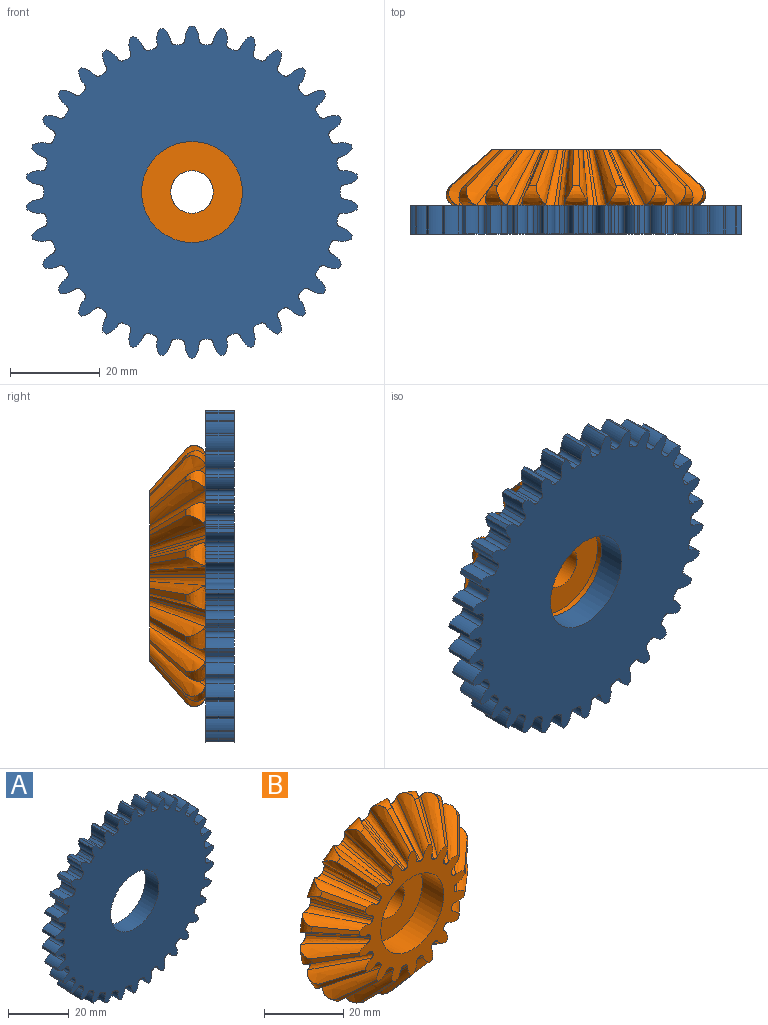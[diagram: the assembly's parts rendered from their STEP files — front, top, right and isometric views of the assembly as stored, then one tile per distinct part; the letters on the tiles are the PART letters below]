
ASSEMBLY  parts=2 mates=1
PART A: 207 faces, bbox 73.8x6.4x74 mm
  f0: cylinder r=33mm len=6.35mm, axis (0,1,0), area 7mm2, adj f34,f35,f40,f204
  f1: cylinder r=33mm len=6.35mm, axis (0,1,0), area 7mm2, adj f34,f35,f199,f205
  f2: cylinder r=33mm len=6.35mm, axis (0,1,0), area 7mm2, adj f34,f35,f194,f200
  f3: cylinder r=33mm len=6.35mm, axis (0,1,0), area 7mm2, adj f34,f35,f189,f195
  f4: cylinder r=33mm len=6.35mm, axis (0,1,0), area 7mm2, adj f34,f35,f184,f190
  f5: cylinder r=33mm len=6.35mm, axis (0,1,0), area 7mm2, adj f34,f35,f179,f185
  f6: cylinder r=33mm len=6.35mm, axis (0,1,0), area 7mm2, adj f34,f35,f174,f180
  f7: cylinder r=33mm len=6.35mm, axis (0,1,0), area 7mm2, adj f34,f35,f169,f175
  f8: cylinder r=33mm len=6.35mm, axis (0,1,0), area 7mm2, adj f34,f35,f164,f170
  f9: cylinder r=33mm len=6.35mm, axis (0,1,0), area 7mm2, adj f34,f35,f159,f165
  f10: cylinder r=33mm len=6.35mm, axis (0,1,0), area 7mm2, adj f34,f35,f154,f160
  f11: cylinder r=33mm len=6.35mm, axis (0,1,0), area 7mm2, adj f34,f35,f149,f155
  f12: cylinder r=33mm len=6.35mm, axis (0,1,0), area 7mm2, adj f34,f35,f144,f150
  f13: cylinder r=33mm len=6.35mm, axis (0,1,0), area 7mm2, adj f34,f35,f139,f145
  f14: cylinder r=33mm len=6.35mm, axis (0,1,0), area 7mm2, adj f34,f35,f134,f140
  f15: cylinder r=33mm len=6.35mm, axis (0,1,0), area 7mm2, adj f34,f35,f129,f135
  f16: cylinder r=33mm len=6.35mm, axis (0,1,0), area 7mm2, adj f34,f35,f124,f130
  f17: cylinder r=33mm len=6.35mm, axis (0,1,0), area 7mm2, adj f34,f35,f119,f125
  f18: cylinder r=33mm len=6.35mm, axis (0,1,0), area 7mm2, adj f34,f35,f114,f120
  f19: cylinder r=33mm len=6.35mm, axis (0,1,0), area 7mm2, adj f34,f35,f109,f115
  f20: cylinder r=33mm len=6.35mm, axis (0,1,0), area 7mm2, adj f34,f35,f104,f110
  f21: cylinder r=33mm len=6.35mm, axis (0,1,0), area 7mm2, adj f34,f35,f99,f105
  f22: cylinder r=33mm len=6.35mm, axis (0,1,0), area 7mm2, adj f34,f35,f94,f100
  f23: cylinder r=33mm len=6.35mm, axis (0,1,0), area 7mm2, adj f34,f35,f89,f95
  f24: cylinder r=33mm len=6.35mm, axis (0,1,0), area 7mm2, adj f34,f35,f84,f90
  f25: cylinder r=33mm len=6.35mm, axis (0,1,0), area 7mm2, adj f34,f35,f79,f85
  f26: cylinder r=33mm len=6.35mm, axis (0,1,0), area 7mm2, adj f34,f35,f74,f80
  f27: cylinder r=33mm len=6.35mm, axis (0,1,0), area 7mm2, adj f34,f35,f69,f75
  f28: cylinder r=33mm len=6.35mm, axis (0,1,0), area 7mm2, adj f34,f35,f64,f70
  f29: cylinder r=33mm len=6.35mm, axis (0,1,0), area 7mm2, adj f34,f35,f59,f65
  f30: cylinder r=33mm len=6.35mm, axis (0,1,0), area 7mm2, adj f34,f35,f54,f60
  f31: cylinder r=33mm len=6.35mm, axis (0,1,0), area 7mm2, adj f34,f35,f49,f55
  f32: cylinder r=33mm len=6.35mm, axis (0,1,0), area 7mm2, adj f34,f35,f44,f50
  f33: cylinder r=33mm len=6.35mm, axis (0,1,0), area 7mm2, adj f34,f35,f39,f45
  f34: plane 74x73.76mm, normal (0,-1,0), area 3393.5mm2, adj f0,f1,f2,f3,f4,f5,f6,f7
  f35: plane 74x73.76mm, normal (0,1,0), area 3393.5mm2, adj f0,f1,f2,f3,f4,f5,f6,f7
  f36: cylinder r=4.53mm len=6.35mm, axis (0,1,0), area 21.2mm2, adj f34,f35,f37,f40
  f37: cylinder r=37mm len=6.35mm, axis (0,1,0), area 5.8mm2, adj f34,f35,f36,f38
  f38: cylinder r=4.53mm len=6.35mm, axis (0,1,0), area 21.2mm2, adj f34,f35,f37,f39
  f39: cylinder r=1mm len=6.35mm, axis (0,1,0), area 9.6mm2, adj f33,f34,f35,f38
  f40: cylinder r=1mm len=6.35mm, axis (0,1,0), area 9.6mm2, adj f0,f34,f35,f36
  f41: cylinder r=4.53mm len=6.35mm, axis (0,1,0), area 21.2mm2, adj f34,f35,f42,f45
  f42: cylinder r=37mm len=6.35mm, axis (0,1,0), area 5.8mm2, adj f34,f35,f41,f43
  f43: cylinder r=4.53mm len=6.35mm, axis (0,1,0), area 21.2mm2, adj f34,f35,f42,f44
  f44: cylinder r=1mm len=6.35mm, axis (0,1,0), area 9.6mm2, adj f32,f34,f35,f43
  f45: cylinder r=1mm len=6.35mm, axis (0,1,0), area 9.6mm2, adj f33,f34,f35,f41
  f46: cylinder r=4.53mm len=6.35mm, axis (0,1,0), area 21.2mm2, adj f34,f35,f47,f50
  f47: cylinder r=37mm len=6.35mm, axis (0,1,0), area 5.8mm2, adj f34,f35,f46,f48
  f48: cylinder r=4.53mm len=6.35mm, axis (0,1,0), area 21.2mm2, adj f34,f35,f47,f49
  f49: cylinder r=1mm len=6.35mm, axis (0,1,0), area 9.6mm2, adj f31,f34,f35,f48
  f50: cylinder r=1mm len=6.35mm, axis (0,1,0), area 9.6mm2, adj f32,f34,f35,f46
  f51: cylinder r=4.53mm len=6.35mm, axis (0,1,0), area 21.2mm2, adj f34,f35,f52,f55
  f52: cylinder r=37mm len=6.35mm, axis (0,1,0), area 5.8mm2, adj f34,f35,f51,f53
  f53: cylinder r=4.53mm len=6.35mm, axis (0,1,0), area 21.2mm2, adj f34,f35,f52,f54
  f54: cylinder r=1mm len=6.35mm, axis (0,1,0), area 9.6mm2, adj f30,f34,f35,f53
  f55: cylinder r=1mm len=6.35mm, axis (0,1,0), area 9.6mm2, adj f31,f34,f35,f51
  f56: cylinder r=4.53mm len=6.35mm, axis (0,1,0), area 21.2mm2, adj f34,f35,f57,f60
  f57: cylinder r=37mm len=6.35mm, axis (0,1,0), area 5.8mm2, adj f34,f35,f56,f58
  f58: cylinder r=4.53mm len=6.35mm, axis (0,1,0), area 21.2mm2, adj f34,f35,f57,f59
  f59: cylinder r=1mm len=6.35mm, axis (0,1,0), area 9.6mm2, adj f29,f34,f35,f58
  f60: cylinder r=1mm len=6.35mm, axis (0,1,0), area 9.6mm2, adj f30,f34,f35,f56
  f61: cylinder r=4.53mm len=6.35mm, axis (0,1,0), area 21.2mm2, adj f34,f35,f62,f65
  f62: cylinder r=37mm len=6.35mm, axis (0,1,0), area 5.8mm2, adj f34,f35,f61,f63
  f63: cylinder r=4.53mm len=6.35mm, axis (0,1,0), area 21.2mm2, adj f34,f35,f62,f64
  f64: cylinder r=1mm len=6.35mm, axis (0,1,0), area 9.6mm2, adj f28,f34,f35,f63
  f65: cylinder r=1mm len=6.35mm, axis (0,1,0), area 9.6mm2, adj f29,f34,f35,f61
  f66: cylinder r=4.53mm len=6.35mm, axis (0,1,0), area 21.2mm2, adj f34,f35,f67,f70
  f67: cylinder r=37mm len=6.35mm, axis (0,1,0), area 5.8mm2, adj f34,f35,f66,f68
  f68: cylinder r=4.53mm len=6.35mm, axis (0,1,0), area 21.2mm2, adj f34,f35,f67,f69
  f69: cylinder r=1mm len=6.35mm, axis (0,1,0), area 9.6mm2, adj f27,f34,f35,f68
  f70: cylinder r=1mm len=6.35mm, axis (0,1,0), area 9.6mm2, adj f28,f34,f35,f66
  f71: cylinder r=4.53mm len=6.35mm, axis (0,1,0), area 21.2mm2, adj f34,f35,f72,f75
  f72: cylinder r=37mm len=6.35mm, axis (0,1,0), area 5.8mm2, adj f34,f35,f71,f73
  f73: cylinder r=4.53mm len=6.35mm, axis (0,1,0), area 21.2mm2, adj f34,f35,f72,f74
  f74: cylinder r=1mm len=6.35mm, axis (0,1,0), area 9.6mm2, adj f26,f34,f35,f73
  f75: cylinder r=1mm len=6.35mm, axis (0,1,0), area 9.6mm2, adj f27,f34,f35,f71
  f76: cylinder r=4.53mm len=6.35mm, axis (0,1,0), area 21.2mm2, adj f34,f35,f77,f80
  f77: cylinder r=37mm len=6.35mm, axis (0,1,0), area 5.8mm2, adj f34,f35,f76,f78
  f78: cylinder r=4.53mm len=6.35mm, axis (0,1,0), area 21.2mm2, adj f34,f35,f77,f79
  f79: cylinder r=1mm len=6.35mm, axis (0,1,0), area 9.6mm2, adj f25,f34,f35,f78
  f80: cylinder r=1mm len=6.35mm, axis (0,1,0), area 9.6mm2, adj f26,f34,f35,f76
  f81: cylinder r=4.53mm len=6.35mm, axis (0,1,0), area 21.2mm2, adj f34,f35,f82,f85
  f82: cylinder r=37mm len=6.35mm, axis (0,1,0), area 5.8mm2, adj f34,f35,f81,f83
  f83: cylinder r=4.53mm len=6.35mm, axis (0,1,0), area 21.2mm2, adj f34,f35,f82,f84
  f84: cylinder r=1mm len=6.35mm, axis (0,1,0), area 9.6mm2, adj f24,f34,f35,f83
  f85: cylinder r=1mm len=6.35mm, axis (0,1,0), area 9.6mm2, adj f25,f34,f35,f81
  f86: cylinder r=4.53mm len=6.35mm, axis (0,1,0), area 21.2mm2, adj f34,f35,f87,f90
  f87: cylinder r=37mm len=6.35mm, axis (0,1,0), area 5.8mm2, adj f34,f35,f86,f88
  f88: cylinder r=4.53mm len=6.35mm, axis (0,1,0), area 21.2mm2, adj f34,f35,f87,f89
  f89: cylinder r=1mm len=6.35mm, axis (0,1,0), area 9.6mm2, adj f23,f34,f35,f88
  f90: cylinder r=1mm len=6.35mm, axis (0,1,0), area 9.6mm2, adj f24,f34,f35,f86
  f91: cylinder r=4.53mm len=6.35mm, axis (0,1,0), area 21.2mm2, adj f34,f35,f92,f95
  f92: cylinder r=37mm len=6.35mm, axis (0,1,0), area 5.8mm2, adj f34,f35,f91,f93
  f93: cylinder r=4.53mm len=6.35mm, axis (0,1,0), area 21.2mm2, adj f34,f35,f92,f94
  f94: cylinder r=1mm len=6.35mm, axis (0,1,0), area 9.6mm2, adj f22,f34,f35,f93
  f95: cylinder r=1mm len=6.35mm, axis (0,1,0), area 9.6mm2, adj f23,f34,f35,f91
  f96: cylinder r=4.53mm len=6.35mm, axis (0,1,0), area 21.2mm2, adj f34,f35,f97,f100
  f97: cylinder r=37mm len=6.35mm, axis (0,1,0), area 5.8mm2, adj f34,f35,f96,f98
  f98: cylinder r=4.53mm len=6.35mm, axis (0,1,0), area 21.2mm2, adj f34,f35,f97,f99
  f99: cylinder r=1mm len=6.35mm, axis (0,1,0), area 9.6mm2, adj f21,f34,f35,f98
  f100: cylinder r=1mm len=6.35mm, axis (0,1,0), area 9.6mm2, adj f22,f34,f35,f96
  f101: cylinder r=4.53mm len=6.35mm, axis (0,1,0), area 21.2mm2, adj f34,f35,f102,f105
  f102: cylinder r=37mm len=6.35mm, axis (0,1,0), area 5.8mm2, adj f34,f35,f101,f103
  f103: cylinder r=4.53mm len=6.35mm, axis (0,1,0), area 21.2mm2, adj f34,f35,f102,f104
  f104: cylinder r=1mm len=6.35mm, axis (0,1,0), area 9.6mm2, adj f20,f34,f35,f103
  f105: cylinder r=1mm len=6.35mm, axis (0,1,0), area 9.6mm2, adj f21,f34,f35,f101
  f106: cylinder r=4.53mm len=6.35mm, axis (0,1,0), area 21.2mm2, adj f34,f35,f107,f110
  f107: cylinder r=37mm len=6.35mm, axis (0,1,0), area 5.8mm2, adj f34,f35,f106,f108
  f108: cylinder r=4.53mm len=6.35mm, axis (0,1,0), area 21.2mm2, adj f34,f35,f107,f109
  f109: cylinder r=1mm len=6.35mm, axis (0,1,0), area 9.6mm2, adj f19,f34,f35,f108
  f110: cylinder r=1mm len=6.35mm, axis (0,1,0), area 9.6mm2, adj f20,f34,f35,f106
  f111: cylinder r=4.53mm len=6.35mm, axis (0,1,0), area 21.2mm2, adj f34,f35,f112,f115
  f112: cylinder r=37mm len=6.35mm, axis (0,1,0), area 5.8mm2, adj f34,f35,f111,f113
  f113: cylinder r=4.53mm len=6.35mm, axis (0,1,0), area 21.2mm2, adj f34,f35,f112,f114
  f114: cylinder r=1mm len=6.35mm, axis (0,1,0), area 9.6mm2, adj f18,f34,f35,f113
  f115: cylinder r=1mm len=6.35mm, axis (0,1,0), area 9.6mm2, adj f19,f34,f35,f111
  f116: cylinder r=4.53mm len=6.35mm, axis (0,1,0), area 21.2mm2, adj f34,f35,f117,f120
  f117: cylinder r=37mm len=6.35mm, axis (0,1,0), area 5.8mm2, adj f34,f35,f116,f118
  f118: cylinder r=4.53mm len=6.35mm, axis (0,1,0), area 21.2mm2, adj f34,f35,f117,f119
  f119: cylinder r=1mm len=6.35mm, axis (0,1,0), area 9.6mm2, adj f17,f34,f35,f118
  f120: cylinder r=1mm len=6.35mm, axis (0,1,0), area 9.6mm2, adj f18,f34,f35,f116
  f121: cylinder r=4.53mm len=6.35mm, axis (0,1,0), area 21.2mm2, adj f34,f35,f122,f125
  f122: cylinder r=37mm len=6.35mm, axis (0,1,0), area 5.8mm2, adj f34,f35,f121,f123
  f123: cylinder r=4.53mm len=6.35mm, axis (0,1,0), area 21.2mm2, adj f34,f35,f122,f124
  f124: cylinder r=1mm len=6.35mm, axis (0,1,0), area 9.6mm2, adj f16,f34,f35,f123
  f125: cylinder r=1mm len=6.35mm, axis (0,1,0), area 9.6mm2, adj f17,f34,f35,f121
  f126: cylinder r=4.53mm len=6.35mm, axis (0,1,0), area 21.2mm2, adj f34,f35,f127,f130
  f127: cylinder r=37mm len=6.35mm, axis (0,1,0), area 5.8mm2, adj f34,f35,f126,f128
  f128: cylinder r=4.53mm len=6.35mm, axis (0,1,0), area 21.2mm2, adj f34,f35,f127,f129
  f129: cylinder r=1mm len=6.35mm, axis (0,1,0), area 9.6mm2, adj f15,f34,f35,f128
  f130: cylinder r=1mm len=6.35mm, axis (0,1,0), area 9.6mm2, adj f16,f34,f35,f126
  f131: cylinder r=4.53mm len=6.35mm, axis (0,1,0), area 21.2mm2, adj f34,f35,f132,f135
  f132: cylinder r=37mm len=6.35mm, axis (0,1,0), area 5.8mm2, adj f34,f35,f131,f133
  f133: cylinder r=4.53mm len=6.35mm, axis (0,1,0), area 21.2mm2, adj f34,f35,f132,f134
  f134: cylinder r=1mm len=6.35mm, axis (0,1,0), area 9.6mm2, adj f14,f34,f35,f133
  f135: cylinder r=1mm len=6.35mm, axis (0,1,0), area 9.6mm2, adj f15,f34,f35,f131
  f136: cylinder r=4.53mm len=6.35mm, axis (0,1,0), area 21.2mm2, adj f34,f35,f137,f140
  f137: cylinder r=37mm len=6.35mm, axis (0,1,0), area 5.8mm2, adj f34,f35,f136,f138
  f138: cylinder r=4.53mm len=6.35mm, axis (0,1,0), area 21.2mm2, adj f34,f35,f137,f139
  f139: cylinder r=1mm len=6.35mm, axis (0,1,0), area 9.6mm2, adj f13,f34,f35,f138
  f140: cylinder r=1mm len=6.35mm, axis (0,1,0), area 9.6mm2, adj f14,f34,f35,f136
  f141: cylinder r=4.53mm len=6.35mm, axis (0,1,0), area 21.2mm2, adj f34,f35,f142,f145
  f142: cylinder r=37mm len=6.35mm, axis (0,1,0), area 5.8mm2, adj f34,f35,f141,f143
  f143: cylinder r=4.53mm len=6.35mm, axis (0,1,0), area 21.2mm2, adj f34,f35,f142,f144
  f144: cylinder r=1mm len=6.35mm, axis (0,1,0), area 9.6mm2, adj f12,f34,f35,f143
  f145: cylinder r=1mm len=6.35mm, axis (0,1,0), area 9.6mm2, adj f13,f34,f35,f141
  f146: cylinder r=4.53mm len=6.35mm, axis (0,1,0), area 21.2mm2, adj f34,f35,f147,f150
  f147: cylinder r=37mm len=6.35mm, axis (0,1,0), area 5.8mm2, adj f34,f35,f146,f148
  f148: cylinder r=4.53mm len=6.35mm, axis (0,1,0), area 21.2mm2, adj f34,f35,f147,f149
  f149: cylinder r=1mm len=6.35mm, axis (0,1,0), area 9.6mm2, adj f11,f34,f35,f148
  f150: cylinder r=1mm len=6.35mm, axis (0,1,0), area 9.6mm2, adj f12,f34,f35,f146
  f151: cylinder r=4.53mm len=6.35mm, axis (0,1,0), area 21.2mm2, adj f34,f35,f152,f155
  f152: cylinder r=37mm len=6.35mm, axis (0,1,0), area 5.8mm2, adj f34,f35,f151,f153
  f153: cylinder r=4.53mm len=6.35mm, axis (0,1,0), area 21.2mm2, adj f34,f35,f152,f154
  f154: cylinder r=1mm len=6.35mm, axis (0,1,0), area 9.6mm2, adj f10,f34,f35,f153
  f155: cylinder r=1mm len=6.35mm, axis (0,1,0), area 9.6mm2, adj f11,f34,f35,f151
  f156: cylinder r=4.53mm len=6.35mm, axis (0,1,0), area 21.2mm2, adj f34,f35,f157,f160
  f157: cylinder r=37mm len=6.35mm, axis (0,1,0), area 5.8mm2, adj f34,f35,f156,f158
  f158: cylinder r=4.53mm len=6.35mm, axis (0,1,0), area 21.2mm2, adj f34,f35,f157,f159
  f159: cylinder r=1mm len=6.35mm, axis (0,1,0), area 9.6mm2, adj f9,f34,f35,f158
  f160: cylinder r=1mm len=6.35mm, axis (0,1,0), area 9.6mm2, adj f10,f34,f35,f156
  f161: cylinder r=4.53mm len=6.35mm, axis (0,1,0), area 21.2mm2, adj f34,f35,f162,f165
  f162: cylinder r=37mm len=6.35mm, axis (0,1,0), area 5.8mm2, adj f34,f35,f161,f163
  f163: cylinder r=4.53mm len=6.35mm, axis (0,1,0), area 21.2mm2, adj f34,f35,f162,f164
  f164: cylinder r=1mm len=6.35mm, axis (0,1,0), area 9.6mm2, adj f8,f34,f35,f163
  f165: cylinder r=1mm len=6.35mm, axis (0,1,0), area 9.6mm2, adj f9,f34,f35,f161
  f166: cylinder r=4.53mm len=6.35mm, axis (0,1,0), area 21.2mm2, adj f34,f35,f167,f170
  f167: cylinder r=37mm len=6.35mm, axis (0,1,0), area 5.8mm2, adj f34,f35,f166,f168
  f168: cylinder r=4.53mm len=6.35mm, axis (0,1,0), area 21.2mm2, adj f34,f35,f167,f169
  f169: cylinder r=1mm len=6.35mm, axis (0,1,0), area 9.6mm2, adj f7,f34,f35,f168
  f170: cylinder r=1mm len=6.35mm, axis (0,1,0), area 9.6mm2, adj f8,f34,f35,f166
  f171: cylinder r=4.53mm len=6.35mm, axis (0,1,0), area 21.2mm2, adj f34,f35,f172,f175
  f172: cylinder r=37mm len=6.35mm, axis (0,1,0), area 5.8mm2, adj f34,f35,f171,f173
  f173: cylinder r=4.53mm len=6.35mm, axis (0,1,0), area 21.2mm2, adj f34,f35,f172,f174
  f174: cylinder r=1mm len=6.35mm, axis (0,1,0), area 9.6mm2, adj f6,f34,f35,f173
  f175: cylinder r=1mm len=6.35mm, axis (0,1,0), area 9.6mm2, adj f7,f34,f35,f171
  f176: cylinder r=4.53mm len=6.35mm, axis (0,1,0), area 21.2mm2, adj f34,f35,f177,f180
  f177: cylinder r=37mm len=6.35mm, axis (0,1,0), area 5.8mm2, adj f34,f35,f176,f178
  f178: cylinder r=4.53mm len=6.35mm, axis (0,1,0), area 21.2mm2, adj f34,f35,f177,f179
  f179: cylinder r=1mm len=6.35mm, axis (0,1,0), area 9.6mm2, adj f5,f34,f35,f178
  f180: cylinder r=1mm len=6.35mm, axis (0,1,0), area 9.6mm2, adj f6,f34,f35,f176
  f181: cylinder r=4.53mm len=6.35mm, axis (0,1,0), area 21.2mm2, adj f34,f35,f182,f185
  f182: cylinder r=37mm len=6.35mm, axis (0,1,0), area 5.8mm2, adj f34,f35,f181,f183
  f183: cylinder r=4.53mm len=6.35mm, axis (0,1,0), area 21.2mm2, adj f34,f35,f182,f184
  f184: cylinder r=1mm len=6.35mm, axis (0,1,0), area 9.6mm2, adj f4,f34,f35,f183
  f185: cylinder r=1mm len=6.35mm, axis (0,1,0), area 9.6mm2, adj f5,f34,f35,f181
  f186: cylinder r=4.53mm len=6.35mm, axis (0,1,0), area 21.2mm2, adj f34,f35,f187,f190
  f187: cylinder r=37mm len=6.35mm, axis (0,1,0), area 5.8mm2, adj f34,f35,f186,f188
  f188: cylinder r=4.53mm len=6.35mm, axis (0,1,0), area 21.2mm2, adj f34,f35,f187,f189
  f189: cylinder r=1mm len=6.35mm, axis (0,1,0), area 9.6mm2, adj f3,f34,f35,f188
  f190: cylinder r=1mm len=6.35mm, axis (0,1,0), area 9.6mm2, adj f4,f34,f35,f186
  f191: cylinder r=4.53mm len=6.35mm, axis (0,1,0), area 21.2mm2, adj f34,f35,f192,f195
  f192: cylinder r=37mm len=6.35mm, axis (0,1,0), area 5.8mm2, adj f34,f35,f191,f193
  f193: cylinder r=4.53mm len=6.35mm, axis (0,1,0), area 21.2mm2, adj f34,f35,f192,f194
  f194: cylinder r=1mm len=6.35mm, axis (0,1,0), area 9.6mm2, adj f2,f34,f35,f193
  f195: cylinder r=1mm len=6.35mm, axis (0,1,0), area 9.6mm2, adj f3,f34,f35,f191
  f196: cylinder r=4.53mm len=6.35mm, axis (0,1,0), area 21.2mm2, adj f34,f35,f197,f200
  f197: cylinder r=37mm len=6.35mm, axis (0,1,0), area 5.8mm2, adj f34,f35,f196,f198
  f198: cylinder r=4.53mm len=6.35mm, axis (0,1,0), area 21.2mm2, adj f34,f35,f197,f199
  f199: cylinder r=1mm len=6.35mm, axis (0,1,0), area 9.6mm2, adj f1,f34,f35,f198
  f200: cylinder r=1mm len=6.35mm, axis (0,1,0), area 9.6mm2, adj f2,f34,f35,f196
  f201: cylinder r=4.53mm len=6.35mm, axis (0,1,0), area 21.2mm2, adj f34,f35,f202,f205
  f202: cylinder r=37mm len=6.35mm, axis (0,1,0), area 5.8mm2, adj f34,f35,f201,f203
  f203: cylinder r=4.53mm len=6.35mm, axis (0,1,0), area 21.2mm2, adj f34,f35,f202,f204
  f204: cylinder r=1mm len=6.35mm, axis (0,1,0), area 9.6mm2, adj f0,f34,f35,f203
  f205: cylinder r=1mm len=6.35mm, axis (0,1,0), area 9.6mm2, adj f1,f34,f35,f201
  f206: cylinder r=11.24mm len=22.48mm, axis (0,-1,0), area 448.4mm2, adj f34,f35
PART B: 133 faces, bbox 66.8x12.7x66.6 mm
  f0: cylinder r=4.76mm len=9.53mm, axis (0,-1,0), area 107.9mm2, adj f129,f131
  f1: cone r=14.88mm half-angle=40deg, axis (0,1,0), area 10.1mm2, adj f2,f8,f10,f124
  f2: bspline ~12.5x12.39mm, area 30.1mm2, adj f1,f7,f8,f9,f10
  f3: cone r=14.88mm half-angle=40deg, axis (0,1,0), area 10.1mm2, adj f4,f8,f10,f11
  f4: bspline ~12.65x12.52mm, area 30mm2, adj f3,f5,f8,f9,f10
  f5: bspline ~17.54x12.65mm, area 50.6mm2, adj f4,f6,f9,f10
  f6: bspline ~14.42x12.65mm, area 17.3mm2, adj f5,f7,f9,f10
  f7: bspline ~17.53x12.65mm, area 50.8mm2, adj f2,f6,f9,f10
  f8: plane 53.14x53.13mm, normal (0,1,0), area 1767.4mm2, adj f1,f2,f3,f4,f9,f11,f12,f13
  f9: bspline ~8.22x6.85mm, area 23mm2, adj f2,f4,f5,f6,f7,f8
  f10: plane 38.16x37.77mm, normal (0,-1,0), area 513mm2, adj f1,f2,f3,f4,f5,f6,f7,f11
  f11: bspline ~12.5x11.74mm, area 30.1mm2, adj f3,f8,f10,f16,f17
  f12: cone r=14.88mm half-angle=40deg, axis (0,1,0), area 10.1mm2, adj f8,f10,f13,f18
  f13: bspline ~12.65x11.67mm, area 30mm2, adj f8,f10,f12,f14,f17
  f14: bspline ~16.67x12.65mm, area 50.6mm2, adj f10,f13,f15,f17
  f15: bspline ~14.08x12.65mm, area 17.3mm2, adj f10,f14,f16,f17
  f16: bspline ~16.29x12.65mm, area 50.8mm2, adj f10,f11,f15,f17
  f17: bspline ~9.84x9.08mm, area 23mm2, adj f8,f11,f13,f14,f15,f16
  f18: bspline ~12.5x9.79mm, area 30.1mm2, adj f8,f10,f12,f23,f24
  f19: cone r=14.88mm half-angle=40deg, axis (0,1,0), area 10.1mm2, adj f8,f10,f20,f25
  f20: bspline ~12.5x9.33mm, area 30mm2, adj f8,f10,f19,f21,f24
  f21: bspline ~13.8x12.65mm, area 50.6mm2, adj f10,f20,f22,f24
  f22: bspline ~12.65x12.05mm, area 17.3mm2, adj f10,f21,f23,f24
  f23: bspline ~13.08x12.65mm, area 50.8mm2, adj f10,f18,f22,f24
  f24: bspline ~10.47x10.32mm, area 23mm2, adj f8,f18,f20,f21,f22,f23
  f25: bspline ~12.5x10.61mm, area 30.1mm2, adj f8,f10,f19,f30,f31
  f26: cone r=14.88mm half-angle=40deg, axis (0,1,0), area 10.1mm2, adj f8,f10,f27,f32
  f27: bspline ~12.5x10.91mm, area 30mm2, adj f8,f10,f26,f28,f31
  f28: bspline ~14.91x12.65mm, area 50.6mm2, adj f10,f27,f29,f31
  f29: bspline ~13.23x12.65mm, area 17.3mm2, adj f10,f28,f30,f31
  f30: bspline ~15.46x12.65mm, area 50.8mm2, adj f10,f25,f29,f31
  f31: bspline ~10.31x9.85mm, area 23mm2, adj f8,f25,f27,f28,f29,f30
  f32: bspline ~12.65x12.28mm, area 30.1mm2, adj f8,f10,f26,f37,f38
  f33: cone r=14.88mm half-angle=40deg, axis (0,1,0), area 10.1mm2, adj f8,f10,f34,f39
  f34: bspline ~12.65x12.37mm, area 30mm2, adj f8,f10,f33,f35,f38
  f35: bspline ~16.94x12.42mm, area 50.6mm2, adj f10,f34,f36,f38
  f36: bspline ~14.45x12.65mm, area 17.3mm2, adj f10,f35,f37,f38
  f37: bspline ~17.14x12.41mm, area 50.8mm2, adj f10,f32,f36,f38
  f38: bspline ~9.07x8.03mm, area 23mm2, adj f8,f32,f34,f35,f36,f37
  f39: bspline ~12.65x12.38mm, area 30.1mm2, adj f8,f10,f33,f44,f45
  f40: cone r=14.88mm half-angle=40deg, axis (0,1,0), area 10.1mm2, adj f8,f10,f41,f46
  f41: bspline ~12.5x12.16mm, area 30mm2, adj f8,f10,f40,f42,f45
  f42: bspline ~17.37x12.65mm, area 50.6mm2, adj f10,f41,f43,f45
  f43: bspline ~14.46x12.65mm, area 17.3mm2, adj f10,f42,f44,f45
  f44: bspline ~16.94x12.41mm, area 50.8mm2, adj f10,f39,f43,f45
  f45: bspline ~9.06x8.03mm, area 23mm2, adj f8,f39,f41,f42,f43,f44
  f46: bspline ~12.5x10.92mm, area 30.1mm2, adj f8,f10,f40,f51,f52
  f47: cone r=14.88mm half-angle=40deg, axis (0,1,0), area 10.1mm2, adj f8,f10,f48,f53
  f48: bspline ~12.5x10.61mm, area 30mm2, adj f8,f10,f47,f49,f52
  f49: bspline ~15.47x12.65mm, area 50.6mm2, adj f10,f48,f50,f52
  f50: bspline ~8.66x8.05mm, area 17.3mm2, adj f10,f49,f51,f52
  f51: bspline ~14.7x12.41mm, area 50.8mm2, adj f10,f46,f50,f52
  f52: bspline ~10.31x9.85mm, area 23mm2, adj f8,f46,f48,f49,f50,f51
  f53: bspline ~12.65x9.42mm, area 30.1mm2, adj f8,f10,f47,f58,f59
  f54: cone r=14.88mm half-angle=40deg, axis (0,1,0), area 10.1mm2, adj f8,f10,f55,f60
  f55: bspline ~12.5x9.78mm, area 30mm2, adj f8,f10,f54,f56,f59
  f56: bspline ~13.07x12.65mm, area 50.6mm2, adj f10,f55,f57,f59
  f57: bspline ~12.65x12.01mm, area 17.3mm2, adj f10,f56,f58,f59
  f58: bspline ~13.61x12.41mm, area 50.8mm2, adj f10,f53,f57,f59
  f59: bspline ~10.48x10.32mm, area 23mm2, adj f8,f53,f55,f56,f57,f58
  f60: bspline ~12.65x11.67mm, area 30.1mm2, adj f8,f10,f54,f65,f66
  f61: cone r=14.88mm half-angle=40deg, axis (0,1,0), area 10.1mm2, adj f8,f10,f62,f67
  f62: bspline ~12.5x11.74mm, area 30mm2, adj f8,f10,f61,f63,f66
  f63: bspline ~16.29x12.65mm, area 50.6mm2, adj f10,f62,f64,f66
  f64: bspline ~9.09x8.05mm, area 17.3mm2, adj f10,f63,f65,f66
  f65: bspline ~16.45x12.41mm, area 50.8mm2, adj f10,f60,f64,f66
  f66: bspline ~9.84x9.08mm, area 23mm2, adj f8,f60,f62,f63,f64,f65
  f67: bspline ~12.5x12.39mm, area 30.1mm2, adj f8,f10,f61,f72,f73
  f68: cone r=14.88mm half-angle=40deg, axis (0,1,0), area 10.1mm2, adj f8,f10,f69,f74
  f69: bspline ~12.65x12.52mm, area 30mm2, adj f8,f10,f68,f70,f73
  f70: bspline ~17.54x12.65mm, area 50.6mm2, adj f10,f69,f71,f73
  f71: bspline ~14.42x12.65mm, area 17.3mm2, adj f10,f70,f72,f73
  f72: bspline ~17.53x12.65mm, area 50.8mm2, adj f10,f67,f71,f73
  f73: bspline ~8.22x6.85mm, area 23mm2, adj f8,f67,f69,f70,f71,f72
  f74: bspline ~12.5x11.74mm, area 30.1mm2, adj f8,f10,f68,f79,f80
  f75: cone r=14.88mm half-angle=40deg, axis (0,1,0), area 10.1mm2, adj f8,f10,f76,f81
  f76: bspline ~12.65x11.67mm, area 30mm2, adj f8,f10,f75,f77,f80
  f77: bspline ~16.67x12.65mm, area 50.6mm2, adj f10,f76,f78,f80
  f78: bspline ~14.08x12.65mm, area 17.3mm2, adj f10,f77,f79,f80
  f79: bspline ~16.29x12.65mm, area 50.8mm2, adj f10,f74,f78,f80
  f80: bspline ~9.84x9.08mm, area 23mm2, adj f8,f74,f76,f77,f78,f79
  f81: bspline ~12.5x9.79mm, area 30.1mm2, adj f8,f10,f75,f86,f87
  f82: cone r=14.88mm half-angle=40deg, axis (0,1,0), area 10.1mm2, adj f8,f10,f83,f88
  f83: bspline ~12.5x9.33mm, area 30mm2, adj f8,f10,f82,f84,f87
  f84: bspline ~13.8x12.65mm, area 50.6mm2, adj f10,f83,f85,f87
  f85: bspline ~12.65x12.05mm, area 17.3mm2, adj f10,f84,f86,f87
  f86: bspline ~13.08x12.65mm, area 50.8mm2, adj f10,f81,f85,f87
  f87: bspline ~10.47x10.32mm, area 23mm2, adj f8,f81,f83,f84,f85,f86
  f88: bspline ~12.5x10.61mm, area 30.1mm2, adj f8,f10,f82,f93,f94
  f89: cone r=14.88mm half-angle=40deg, axis (0,1,0), area 10.1mm2, adj f8,f10,f90,f95
  f90: bspline ~12.5x10.91mm, area 30mm2, adj f8,f10,f89,f91,f94
  f91: bspline ~14.91x12.65mm, area 50.6mm2, adj f10,f90,f92,f94
  f92: bspline ~13.23x12.65mm, area 17.3mm2, adj f10,f91,f93,f94
  f93: bspline ~15.46x12.65mm, area 50.8mm2, adj f10,f88,f92,f94
  f94: bspline ~10.31x9.85mm, area 23mm2, adj f8,f88,f90,f91,f92,f93
  f95: bspline ~12.65x12.28mm, area 30.1mm2, adj f8,f10,f89,f100,f101
  f96: cone r=14.88mm half-angle=40deg, axis (0,1,0), area 10.1mm2, adj f8,f10,f97,f102
  f97: bspline ~12.65x12.37mm, area 30mm2, adj f8,f10,f96,f98,f101
  f98: bspline ~16.94x12.42mm, area 50.6mm2, adj f10,f97,f99,f101
  f99: bspline ~14.45x12.65mm, area 17.3mm2, adj f10,f98,f100,f101
  f100: bspline ~17.14x12.41mm, area 50.8mm2, adj f10,f95,f99,f101
  f101: bspline ~9.07x8.03mm, area 23mm2, adj f8,f95,f97,f98,f99,f100
  f102: bspline ~12.65x12.38mm, area 30.1mm2, adj f8,f10,f96,f107,f108
  f103: cone r=14.88mm half-angle=40deg, axis (0,1,0), area 10.1mm2, adj f8,f10,f104,f109
  f104: bspline ~12.5x12.16mm, area 30mm2, adj f8,f10,f103,f105,f108
  f105: bspline ~17.37x12.65mm, area 50.6mm2, adj f10,f104,f106,f108
  f106: bspline ~14.46x12.65mm, area 17.3mm2, adj f10,f105,f107,f108
  f107: bspline ~16.94x12.41mm, area 50.8mm2, adj f10,f102,f106,f108
  f108: bspline ~9.06x8.03mm, area 23mm2, adj f8,f102,f104,f105,f106,f107
  f109: bspline ~12.5x10.92mm, area 30.1mm2, adj f8,f10,f103,f114,f115
  f110: cone r=14.88mm half-angle=40deg, axis (0,1,0), area 10.1mm2, adj f8,f10,f111,f116
  f111: bspline ~12.5x10.61mm, area 30mm2, adj f8,f10,f110,f112,f115
  f112: bspline ~15.47x12.65mm, area 50.6mm2, adj f10,f111,f113,f115
  f113: bspline ~8.66x8.05mm, area 17.3mm2, adj f10,f112,f114,f115
  f114: bspline ~14.7x12.41mm, area 50.8mm2, adj f10,f109,f113,f115
  f115: bspline ~10.31x9.85mm, area 23mm2, adj f8,f109,f111,f112,f113,f114
  f116: bspline ~12.65x9.42mm, area 30.1mm2, adj f8,f10,f110,f121,f122
  f117: cone r=14.88mm half-angle=40deg, axis (0,1,0), area 10.1mm2, adj f8,f10,f118,f123
  f118: bspline ~12.5x9.78mm, area 30mm2, adj f8,f10,f117,f119,f122
  f119: bspline ~13.07x12.65mm, area 50.6mm2, adj f10,f118,f120,f122
  f120: bspline ~12.65x12.01mm, area 17.3mm2, adj f10,f119,f121,f122
  f121: bspline ~13.61x12.41mm, area 50.8mm2, adj f10,f116,f120,f122
  f122: bspline ~10.48x10.32mm, area 23mm2, adj f8,f116,f118,f119,f120,f121
  f123: bspline ~12.65x11.67mm, area 30.1mm2, adj f8,f10,f117,f127,f128
  f124: bspline ~12.5x11.74mm, area 30mm2, adj f1,f8,f10,f125,f128
  f125: bspline ~16.29x12.65mm, area 50.6mm2, adj f10,f124,f126,f128
  f126: bspline ~9.09x8.05mm, area 17.3mm2, adj f10,f125,f127,f128
  f127: bspline ~16.45x12.41mm, area 50.8mm2, adj f10,f123,f126,f128
  f128: bspline ~9.84x9.08mm, area 23mm2, adj f8,f123,f124,f125,f126,f127
  f129: plane 22.48x22.48mm, normal (0,-1,0), area 325.6mm2, adj f0,f130
  f130: cylinder r=11.24mm len=22.48mm, axis (0,-1,0), area 538.1mm2, adj f10,f129
  f131: plane 22.48x22.48mm, normal (0,1,0), area 325.6mm2, adj f0,f132
  f132: cylinder r=11.24mm len=22.48mm, axis (0,1,0), area 89.7mm2, adj f8,f131
PLACE A at identity fixed
PLACE B rot(axis=(1,0,0),180deg) t=(0,15.88,0)mm
MATE fastened A.f0 <-> B.f12  axis (0,1,0) through (0,3.18,0)mm
